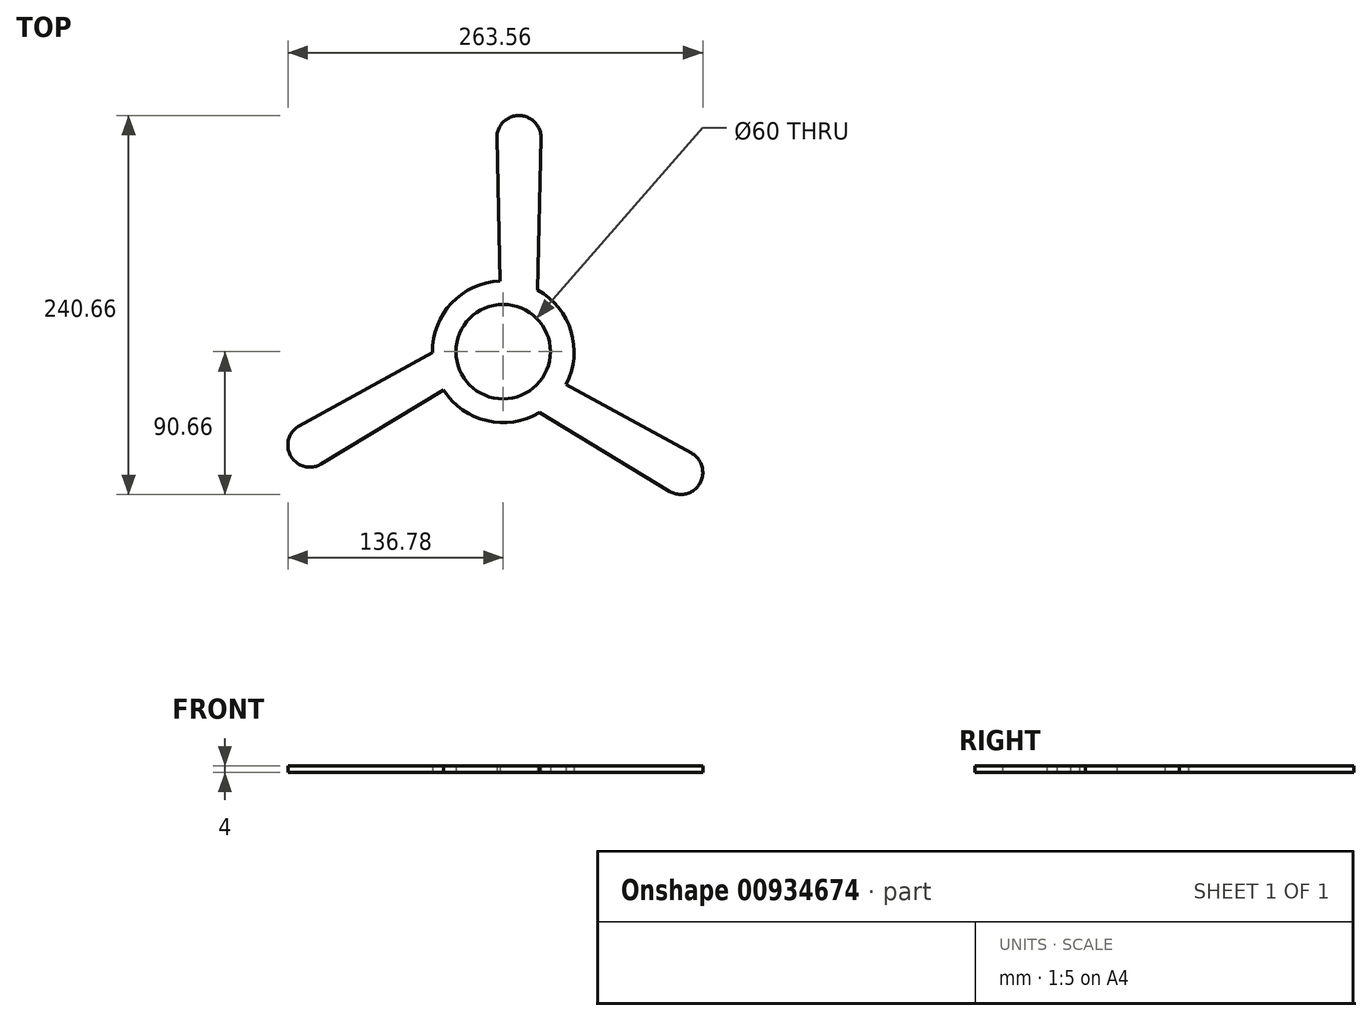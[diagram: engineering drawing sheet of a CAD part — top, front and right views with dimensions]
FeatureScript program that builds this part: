
annotation { "Feature Type Name" : "Feature", "Feature Type Description" : "" }
export const myFeature = defineFeature(function(context is Context, id is Id, definition is map)
    precondition{}
    {
        {
            var Q0;
            Q0=qCreatedBy(makeId("Top.planeOp"),FACE);
            var sketch = newSketch(context, id + "F0", { "sketchPlane" : qUnion([Q0])});
            skCircle(sketch, "E0", {"center": v(0, 0) * mm, "radius": 30 * mm});
            skArc(sketch, "E1", {"start": v(39.96, -20.7) * mm, "mid": v(43.1, 12.95) * mm, "end": v(21.94, 39.29) * mm});
            skLineSegment(sketch, "E2", {"start": v(0, 0) * mm, "end": v(0, 45) * mm, "construction": true});
            skLineSegment(sketch, "E3", {"start": v(-4, 135.7) * mm, "end": v(-2.06, 44.95) * mm});
            skLineSegment(sketch, "E4", {"start": v(24, 135.7) * mm, "end": v(21.94, 39.29) * mm});
            skLineSegment(sketch, "E5", {"start": v(10, 136) * mm, "end": v(10, 43.87) * mm, "construction": true});
            skArc(sketch, "E6", {"start": v(24, 135.7) * mm, "mid": v(10, 150) * mm, "end": v(-4, 135.7) * mm});
            skLineSegment(sketch, "E7", {"start": v(0, 0) * mm, "end": v(45, 0) * mm, "construction": true});
            skArc(sketch, "E8.1.0", {"start": v(105.52, -88.63) * mm, "mid": v(124.9, -83.66) * mm, "end": v(119.52, -64.38) * mm});
            skLineSegment(sketch, "E8.1.1", {"start": v(105.52, -88.63) * mm, "end": v(23.06, -38.64) * mm});
            skLineSegment(sketch, "E8.1.2", {"start": v(112.78, -76.66) * mm, "end": v(33, -30.6) * mm, "construction": true});
            skLineSegment(sketch, "E8.1.3", {"start": v(119.52, -64.38) * mm, "end": v(39.96, -20.7) * mm});
            skArc(sketch, "E8.2.0", {"start": v(-129.52, -47.06) * mm, "mid": v(-134.9, -66.34) * mm, "end": v(-115.52, -71.31) * mm});
            skLineSegment(sketch, "E8.2.1", {"start": v(-129.52, -47.06) * mm, "end": v(-45, -0.64) * mm});
            skLineSegment(sketch, "E8.2.2", {"start": v(-122.78, -59.34) * mm, "end": v(-43, -13.28) * mm, "construction": true});
            skLineSegment(sketch, "E8.2.3", {"start": v(-115.52, -71.31) * mm, "end": v(-37.9, -24.26) * mm});
            skLineSegment(sketch, "E8.anchor1", {"start": v(0, 0) * mm, "end": v(-2.06, 44.95) * mm, "construction": true});
            skLineSegment(sketch, "E8.anchor2", {"start": v(0, 0) * mm, "end": v(-37.9, -24.26) * mm, "construction": true});
            skArc(sketch, "E9.trimOffspring", {"start": v(-37.9, -24.26) * mm, "mid": v(-10.33, -43.8) * mm, "end": v(23.06, -38.64) * mm});
            skArc(sketch, "E10.trimOffspring", {"start": v(-2.06, 44.95) * mm, "mid": v(-32.76, 30.85) * mm, "end": v(-45, -0.64) * mm});
            skSolve(sketch);
        }
        {
            var Q0;
            Q0=qSketchRegion(id+"F0",true);
            extrude(context, id + "F1", {"entities" : qUnion([Q0]), "depth" : 4 * mm, "offsetDistance" : 25 * mm});
        }
    });
